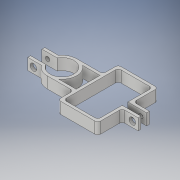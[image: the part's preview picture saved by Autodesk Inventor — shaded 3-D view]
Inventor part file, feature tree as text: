
AUTODESK INVENTOR PART (.ipt)
format: ipt  version: 2018 (Build 220112000, 112)  size: 212,480 bytes
history: native  units: in
note: dims shown in document units (in); Inventor stores cm internally (conversion verified against a paired STEP export)
features: extrude x5, sketch x5, fillet x2
ambient origin geometry x8: Origin, YZ Plane, XZ Plane, XY Plane, X Axis, Y Axis, Z Axis, Center Point
bodies: Solid1 (feature_tree)
feature tree (12):
  extrude  "Extrusion1"  Depth=2.4in
  extrude  "Extrusion2"  Depth=0.125in
  extrude  "Extrusion3"  Depth=0.125in
  fillet  "Fillet1"  Radius=0.125in
  fillet  "Fillet2"  Radius=0.125in
  extrude  "Extrusion4"  Depth=0.7in
  extrude  "Extrusion5"  Depth=0.5in TaperAngle=0.0deg
  sketch  "Sketch1"  dims[d0=1.5in d1=2.4in]
  sketch  "Sketch2"  dims[d2=0.125in d3=0.125in]
  sketch  "Sketch3"  dims[d4=0.125in d5=0.125in d6=0.125in d7=0.125in]
  sketch  "Sketch4"  dims[d8=0.125in d9=0.7in]
  sketch  "Sketch5"  dims[d10=0.25in d11=0.5in d12=0.0in d13=0.193in d14=0.25in d15=0.25in d16=0.9375in d17=0.0in d18=0.05in d19=0.375in d20=0.0in d21=0.125in d22=0.125in d23=1.05in d24=0.125in d25=0.125in d26=0.125in d27=0.6in d28=0.25in d29=0.25in d30=0.125in d31=0.125in d32=0.5in d33=0.125in d34=0.125in d35=0.193in d36=0.25in d37=0.25in d38=0.9375in d39=0.0in d40=0.05in d41=0.375in d42=0.0in]
